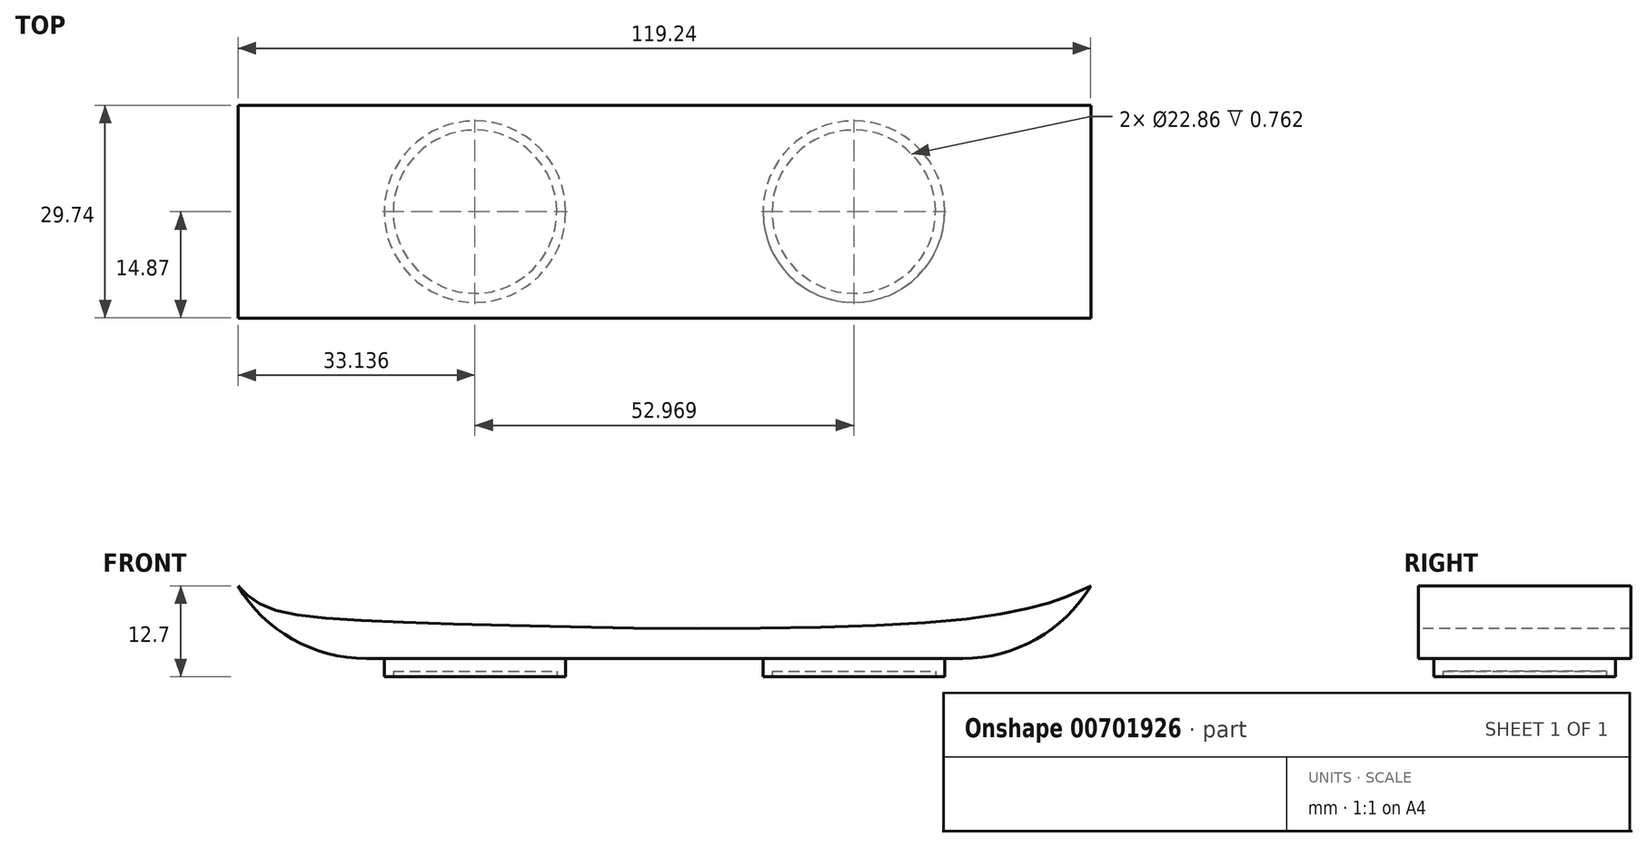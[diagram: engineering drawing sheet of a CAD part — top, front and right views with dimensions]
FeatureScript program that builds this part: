
annotation { "Feature Type Name" : "Feature", "Feature Type Description" : "" }
export const myFeature = defineFeature(function(context is Context, id is Id, definition is map)
    precondition{}
    {
        {
            var Q0;
            Q0=qCreatedBy(makeId("Top.planeOp"),FACE);
            var sketch = newSketch(context, id + "F0", { "sketchPlane" : qUnion([Q0])});
            skLineSegment(sketch, "E0.bottom", {"start": v(59.62, -14.87) * mm, "end": v(-59.62, -14.87) * mm});
            skLineSegment(sketch, "E0.top", {"start": v(59.62, 14.87) * mm, "end": v(-59.62, 14.87) * mm});
            skLineSegment(sketch, "E0.left", {"start": v(59.62, -14.87) * mm, "end": v(59.62, 14.87) * mm});
            skLineSegment(sketch, "E0.right", {"start": v(-59.62, -14.87) * mm, "end": v(-59.62, 14.87) * mm});
            skPoint(sketch, "E0.middle", {"position": v(0, 0) * mm});
            skSolve(sketch);
        }
        {
            var Q0;
            Q0=makeQuery(id+"F0.imprint","IMPRINT",FACE,{"disambiguationData":[TD([[makeQuery(id+"F0.imprint","IMPRINT",EDGE,{"derivedFrom":sQuery(id+"F0.wireOp",EDGE,"E0.bottom")}),-1.0]])]});
            extrude(context, id + "F1", {"entities" : qUnion([Q0]), "depth" : 10.16 * mm, "offsetDistance" : 25.4 * mm});
        }
        {
            var Q0;
            Q0=makeQuery(id+"F1.opExtrude","SWEPT_FACE",FACE,{"disambiguationData":[OSD([sQuery(id+"F0.wireOp",EDGE,"E0.bottom")])]});
            var sketch = newSketch(context, id + "F2", { "sketchPlane" : qUnion([Q0])});
            skPoint(sketch, "E1.2.internal.snap0", {"position": v(-59.62, 5.08) * mm});
            skPoint(sketch, "E1.3.internal.snap0", {"position": v(-59.62, 5.08) * mm});
            skFitSpline(sketch, "E1", {"points": [v(-59.62, 10.16) * mm, v(-56.12, 7.41) * mm, v(-36.6, 5.08) * mm, v(37.53, 5.08) * mm, v(55.42, 8.35) * mm, v(59.62, 10.16) * mm], "startDerivative": vector(29.5, -30.77) * mm, "endDerivative": vector(37.83, 18) * mm});
            skLineSegment(sketch, "E2", {"start": v(-59.62, 10.16) * mm, "end": v(59.62, 10.16) * mm});
            skSolve(sketch);
        }
        {
            var Q0;
            Q0=makeQuery(id+"F2.imprint","IMPRINT",FACE,{"disambiguationData":[TD([[makeQuery(id+"F2.imprint","IMPRINT",EDGE,{"derivedFrom":sQuery(id+"F2.wireOp",EDGE,"E1")}),1.0]])]});
            extrude(context, id + "F3", {"entities" : qUnion([Q0]), "operationType" : NewBodyOperationType.REMOVE, "oppositeDirection" : true, "depth" : 35.05 * mm, "offsetDistance" : 25.4 * mm});
        }
        {
            var Q0;
            Q0=makeQuery(id+"F1.opExtrude","CAP_EDGE",EDGE,{"disambiguationData":[OSD([sQuery(id+"F0.wireOp",EDGE,"E0.left")])],"isStart":true});
            var Q1;
            Q1=makeQuery(id+"F1.opExtrude","CAP_EDGE",EDGE,{"disambiguationData":[OSD([sQuery(id+"F0.wireOp",EDGE,"E0.right")])],"isStart":true});
            fillet(context, id + "F4", {"entities" : qUnion([Q0, Q1]), "radius" : 20.85 * mm, "tangentPropagation" : true, "allowEdgeOverflow" : false});
        }
        {
            var Q0;
            Q0=makeQuery(id+"F1.opExtrude","CAP_FACE",FACE,{"disambiguationData":[OSD([sQuery(id+"F0.wireOp",EDGE,"E0.bottom"),sQuery(id+"F0.wireOp",EDGE,"E0.top"),sQuery(id+"F0.wireOp",EDGE,"E0.left"),sQuery(id+"F0.wireOp",EDGE,"E0.right")])],"isStart":true});
            var sketch = newSketch(context, id + "F5", { "sketchPlane" : qUnion([Q0])});
            skCircle(sketch, "E3", {"center": v(-26.48, 0) * mm, "radius": 12.7 * mm});
            skCircle(sketch, "E4", {"center": v(26.48, 0) * mm, "radius": 12.7 * mm});
            skSolve(sketch);
        }
        {
            var Q0;
            Q0=makeQuery(id+"F5.imprint","IMPRINT",FACE,{"disambiguationData":[TD([[makeQuery(id+"F5.imprint","IMPRINT",EDGE,{"derivedFrom":sQuery(id+"F5.wireOp",EDGE,"E3")}),1.0]])]});
            var Q1;
            Q1=makeQuery(id+"F5.imprint","IMPRINT",FACE,{"disambiguationData":[TD([[makeQuery(id+"F5.imprint","IMPRINT",EDGE,{"derivedFrom":sQuery(id+"F5.wireOp",EDGE,"E4")}),1.0]])]});
            extrude(context, id + "F6", {"entities" : qUnion([Q0, Q1]), "operationType" : NewBodyOperationType.ADD, "depth" : 2.54 * mm, "offsetDistance" : 25.4 * mm});
        }
        {
            var Q0;
            Q0=makeQuery(id+"F6.opExtrude","CAP_FACE",FACE,{"disambiguationData":[OSD([sQuery(id+"F5.wireOp",EDGE,"E3")])],"isStart":false});
            var sketch = newSketch(context, id + "F7", { "sketchPlane" : qUnion([Q0])});
            skCircle(sketch, "E5", {"center": v(-26.48, 0) * mm, "radius": 11.43 * mm});
            skCircle(sketch, "E6", {"center": v(26.48, 0) * mm, "radius": 11.43 * mm});
            skSolve(sketch);
        }
        {
            var Q0;
            Q0=makeQuery(id+"F7.imprint","IMPRINT",FACE,{"disambiguationData":[TD([[makeQuery(id+"F7.imprint","IMPRINT",EDGE,{"derivedFrom":sQuery(id+"F7.wireOp",EDGE,"E5")}),1.0]])]});
            var Q1;
            Q1=makeQuery(id+"F7.imprint","IMPRINT",FACE,{"disambiguationData":[TD([[makeQuery(id+"F7.imprint","IMPRINT",EDGE,{"derivedFrom":sQuery(id+"F7.wireOp",EDGE,"E6")}),1.0]])]});
            extrude(context, id + "F8", {"entities" : qUnion([Q0, Q1]), "operationType" : NewBodyOperationType.REMOVE, "oppositeDirection" : true, "depth" : 0.76 * mm, "offsetDistance" : 25.4 * mm});
        }
    });
